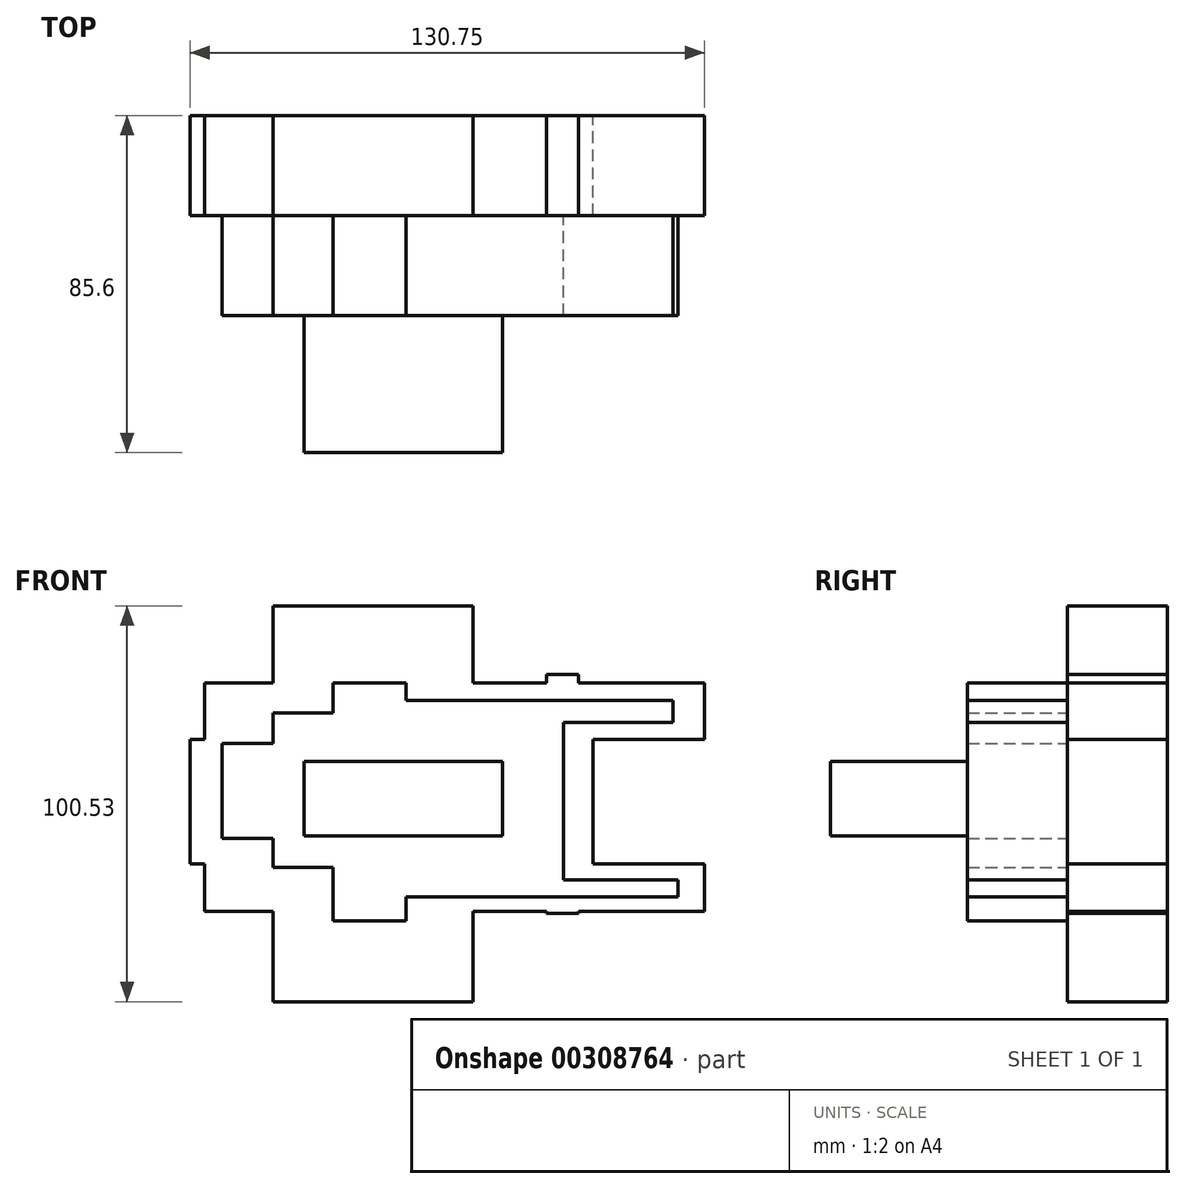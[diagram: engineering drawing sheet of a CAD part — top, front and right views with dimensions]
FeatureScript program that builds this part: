
annotation { "Feature Type Name" : "Feature", "Feature Type Description" : "" }
export const myFeature = defineFeature(function(context is Context, id is Id, definition is map)
    precondition{}
    {
        {
            var Q0;
            Q0=qCreatedBy(makeId("Front.planeOp"),FACE);
            var sketch = newSketch(context, id + "F0", { "sketchPlane" : qUnion([Q0])});
            skLineSegment(sketch, "E0.bottom", {"start": v(-24.95, 46.16) * mm, "end": v(25.85, 46.16) * mm});
            skLineSegment(sketch, "E0.top", {"start": v(-24.95, -54.37) * mm, "end": v(25.85, -54.37) * mm});
            skLineSegment(sketch, "E0.left", {"start": v(-24.95, 46.16) * mm, "end": v(-24.95, 12.2) * mm});
            skLineSegment(sketch, "E0.right", {"start": v(25.85, 46.16) * mm, "end": v(25.85, 12.2) * mm});
            skLineSegment(sketch, "E1.bottom", {"start": v(-46.08, 12.2) * mm, "end": v(-42.33, 12.2) * mm});
            skLineSegment(sketch, "E1.top", {"start": v(-46.08, -19.34) * mm, "end": v(-42.33, -19.34) * mm});
            skLineSegment(sketch, "E1.left", {"start": v(-46.08, 12.2) * mm, "end": v(-46.08, -19.34) * mm});
            skLineSegment(sketch, "E1.right", {"start": v(56.33, 12.2) * mm, "end": v(56.33, -19.34) * mm});
            skLineSegment(sketch, "E2.bottom", {"start": v(44.56, 28.78) * mm, "end": v(52.58, 28.78) * mm});
            skLineSegment(sketch, "E2.top", {"start": v(44.56, -31.91) * mm, "end": v(52.58, -31.91) * mm});
            skLineSegment(sketch, "E2.left", {"start": v(44.56, 28.78) * mm, "end": v(44.56, 12.2) * mm});
            skLineSegment(sketch, "E2.right", {"start": v(52.58, 28.78) * mm, "end": v(52.58, 12.2) * mm});
            skLineSegment(sketch, "E3.bottom", {"start": v(-42.33, 26.64) * mm, "end": v(84.67, 26.64) * mm});
            skLineSegment(sketch, "E3.top", {"start": v(-42.33, -31.38) * mm, "end": v(84.67, -31.38) * mm});
            skLineSegment(sketch, "E3.left", {"start": v(-42.33, 26.64) * mm, "end": v(-42.33, 12.2) * mm});
            skLineSegment(sketch, "E3.right", {"start": v(84.67, 26.64) * mm, "end": v(84.67, 12.2) * mm});
            skLineSegment(sketch, "E4.trimOffspring", {"start": v(-42.33, -19.34) * mm, "end": v(-42.33, -31.38) * mm});
            skLineSegment(sketch, "E5.trimOffspring", {"start": v(84.67, -19.34) * mm, "end": v(84.67, -31.38) * mm});
            skLineSegment(sketch, "E6.trimOffspring", {"start": v(-24.95, 12.2) * mm, "end": v(84.67, 12.2) * mm});
            skLineSegment(sketch, "E7.trimOffspring", {"start": v(-24.95, -19.34) * mm, "end": v(84.67, -19.34) * mm});
            skLineSegment(sketch, "E8.trimOffspring", {"start": v(-24.95, -19.34) * mm, "end": v(-24.95, -54.37) * mm});
            skLineSegment(sketch, "E9.trimOffspring", {"start": v(25.85, -19.34) * mm, "end": v(44.56, -19.34) * mm});
            skLineSegment(sketch, "E10.trimOffspring", {"start": v(25.85, 12.2) * mm, "end": v(44.56, 12.2) * mm});
            skLineSegment(sketch, "E11.trimOffspring", {"start": v(25.85, -19.34) * mm, "end": v(25.85, -54.37) * mm});
            skLineSegment(sketch, "E12.trimOffspring", {"start": v(44.56, -19.34) * mm, "end": v(44.56, -31.91) * mm});
            skLineSegment(sketch, "E13.trimOffspring", {"start": v(52.58, -19.34) * mm, "end": v(52.58, -31.91) * mm});
            skLineSegment(sketch, "E14.trimOffspring", {"start": v(52.58, 12.2) * mm, "end": v(56.33, 12.2) * mm});
            skLineSegment(sketch, "E15.trimOffspring", {"start": v(52.58, -19.34) * mm, "end": v(56.33, -19.34) * mm});
            skSolve(sketch);
        }
        {
            var Q0;
            Q0 = qSketchRegion(id + "F0", true);
            extrude(context, id + "F1", {"entities" : qUnion([Q0]), "depth" : 25.4 * mm});
        }
        {
            var Q0;
            Q0=makeQuery(id+"F1.opExtrude","CAP_FACE",FACE,{"disambiguationData":[OSD([sQuery(id+"F0.wireOp",EDGE,"E0.bottom"),sQuery(id+"F0.wireOp",EDGE,"E0.top"),sQuery(id+"F0.wireOp",EDGE,"E0.left"),sQuery(id+"F0.wireOp",EDGE,"E0.right"),sQuery(id+"F0.wireOp",EDGE,"E1.bottom"),sQuery(id+"F0.wireOp",EDGE,"E1.top"),sQuery(id+"F0.wireOp",EDGE,"E1.left"),sQuery(id+"F0.wireOp",EDGE,"E1.right"),sQuery(id+"F0.wireOp",EDGE,"E2.bottom"),sQuery(id+"F0.wireOp",EDGE,"E2.top"),sQuery(id+"F0.wireOp",EDGE,"E2.left"),sQuery(id+"F0.wireOp",EDGE,"E2.right"),sQuery(id+"F0.wireOp",EDGE,"E3.bottom"),sQuery(id+"F0.wireOp",EDGE,"E3.top"),sQuery(id+"F0.wireOp",EDGE,"E3.left"),sQuery(id+"F0.wireOp",EDGE,"E3.right"),sQuery(id+"F0.wireOp",EDGE,"E4.trimOffspring"),sQuery(id+"F0.wireOp",EDGE,"E5.trimOffspring"),sQuery(id+"F0.wireOp",EDGE,"E6.trimOffspring"),sQuery(id+"F0.wireOp",EDGE,"E7.trimOffspring"),sQuery(id+"F0.wireOp",EDGE,"E8.trimOffspring"),sQuery(id+"F0.wireOp",EDGE,"E11.trimOffspring"),sQuery(id+"F0.wireOp",EDGE,"E12.trimOffspring"),sQuery(id+"F0.wireOp",EDGE,"E13.trimOffspring")])],"isStart":false});
            var sketch = newSketch(context, id + "F2", { "sketchPlane" : qUnion([Q0])});
            skLineSegment(sketch, "E16", {"start": v(-9.7, 26.64) * mm, "end": v(-9.7, 19.04) * mm});
            skLineSegment(sketch, "E17", {"start": v(-9.7, 19.04) * mm, "end": v(-24.95, 19.04) * mm});
            skLineSegment(sketch, "E18", {"start": v(-24.95, 19.04) * mm, "end": v(-24.95, 11.3) * mm});
            skLineSegment(sketch, "E19", {"start": v(-24.95, 11.3) * mm, "end": v(-37.86, 11.3) * mm});
            skLineSegment(sketch, "E20", {"start": v(-37.86, 11.3) * mm, "end": v(-37.86, -12.84) * mm});
            skLineSegment(sketch, "E21", {"start": v(-37.86, -12.84) * mm, "end": v(-24.95, -12.84) * mm});
            skLineSegment(sketch, "E22", {"start": v(-24.95, -12.84) * mm, "end": v(-24.95, -20.27) * mm});
            skLineSegment(sketch, "E23", {"start": v(-24.95, -20.27) * mm, "end": v(-9.7, -20.27) * mm});
            skLineSegment(sketch, "E24", {"start": v(-9.7, -20.27) * mm, "end": v(-9.7, -33.9) * mm});
            skLineSegment(sketch, "E25", {"start": v(-9.7, -33.9) * mm, "end": v(8.88, -33.9) * mm});
            skLineSegment(sketch, "E26", {"start": v(8.88, -33.9) * mm, "end": v(8.88, -27.7) * mm});
            skLineSegment(sketch, "E27", {"start": v(8.88, -27.7) * mm, "end": v(77.9, -27.7) * mm});
            skLineSegment(sketch, "E28", {"start": v(77.9, -27.7) * mm, "end": v(77.9, -23.37) * mm});
            skLineSegment(sketch, "E29", {"start": v(77.9, -23.37) * mm, "end": v(48.8, -23.37) * mm});
            skLineSegment(sketch, "E30", {"start": v(48.8, -23.37) * mm, "end": v(48.8, 16.56) * mm});
            skLineSegment(sketch, "E31", {"start": v(48.8, 16.56) * mm, "end": v(76.66, 16.56) * mm});
            skLineSegment(sketch, "E32", {"start": v(76.66, 16.56) * mm, "end": v(76.66, 22.13) * mm});
            skLineSegment(sketch, "E33", {"start": v(76.66, 22.13) * mm, "end": v(8.88, 22.13) * mm});
            skLineSegment(sketch, "E34", {"start": v(8.88, 22.13) * mm, "end": v(8.88, 26.64) * mm});
            skLineSegment(sketch, "E35", {"start": v(8.88, 26.64) * mm, "end": v(-9.7, 26.64) * mm});
            skSolve(sketch);
        }
        {
            var Q0;
            Q0=makeQuery(id+"F2.imprint","IMPRINT",FACE,{"disambiguationData":[TD([[makeQuery(id+"F2.imprint","IMPRINT",EDGE,{"derivedFrom":sQuery(id+"F2.wireOp",EDGE,"E16")}),1.0]])]});
            extrude(context, id + "F3", {"entities" : qUnion([Q0]), "operationType" : NewBodyOperationType.ADD, "depth" : 25.4 * mm});
        }
        {
            var Q0;
            Q0=makeQuery(id+"F3.opExtrude","CAP_FACE",FACE,{"disambiguationData":[OSD([sQuery(id+"F2.wireOp",EDGE,"E16"),sQuery(id+"F2.wireOp",EDGE,"E17"),sQuery(id+"F2.wireOp",EDGE,"E18"),sQuery(id+"F2.wireOp",EDGE,"E19"),sQuery(id+"F2.wireOp",EDGE,"E20"),sQuery(id+"F2.wireOp",EDGE,"E21"),sQuery(id+"F2.wireOp",EDGE,"E22"),sQuery(id+"F2.wireOp",EDGE,"E23"),sQuery(id+"F2.wireOp",EDGE,"E24"),sQuery(id+"F2.wireOp",EDGE,"E25"),sQuery(id+"F2.wireOp",EDGE,"E26"),sQuery(id+"F2.wireOp",EDGE,"E27"),sQuery(id+"F2.wireOp",EDGE,"E28"),sQuery(id+"F2.wireOp",EDGE,"E29"),sQuery(id+"F2.wireOp",EDGE,"E30"),sQuery(id+"F2.wireOp",EDGE,"E31"),sQuery(id+"F2.wireOp",EDGE,"E32"),sQuery(id+"F2.wireOp",EDGE,"E33"),sQuery(id+"F2.wireOp",EDGE,"E34"),sQuery(id+"F2.wireOp",EDGE,"E35")])],"isStart":false});
            var sketch = newSketch(context, id + "F4", { "sketchPlane" : qUnion([Q0])});
            skLineSegment(sketch, "E36.bottom", {"start": v(-17.12, 6.65) * mm, "end": v(33.33, 6.65) * mm});
            skLineSegment(sketch, "E36.top", {"start": v(-17.12, -12.23) * mm, "end": v(33.33, -12.23) * mm});
            skLineSegment(sketch, "E36.left", {"start": v(-17.12, 6.65) * mm, "end": v(-17.12, -12.23) * mm});
            skLineSegment(sketch, "E36.right", {"start": v(33.33, 6.65) * mm, "end": v(33.33, -12.23) * mm});
            skSolve(sketch);
        }
        {
            var Q0;
            Q0=makeQuery(id+"F4.imprint","IMPRINT",FACE,{"disambiguationData":[TD([[makeQuery(id+"F4.imprint","IMPRINT",EDGE,{"derivedFrom":sQuery(id+"F4.wireOp",EDGE,"E36.bottom")}),-1.0]])]});
            extrude(context, id + "F5", {"entities" : qUnion([Q0]), "operationType" : NewBodyOperationType.ADD, "depth" : 34.8 * mm});
        }
    });
